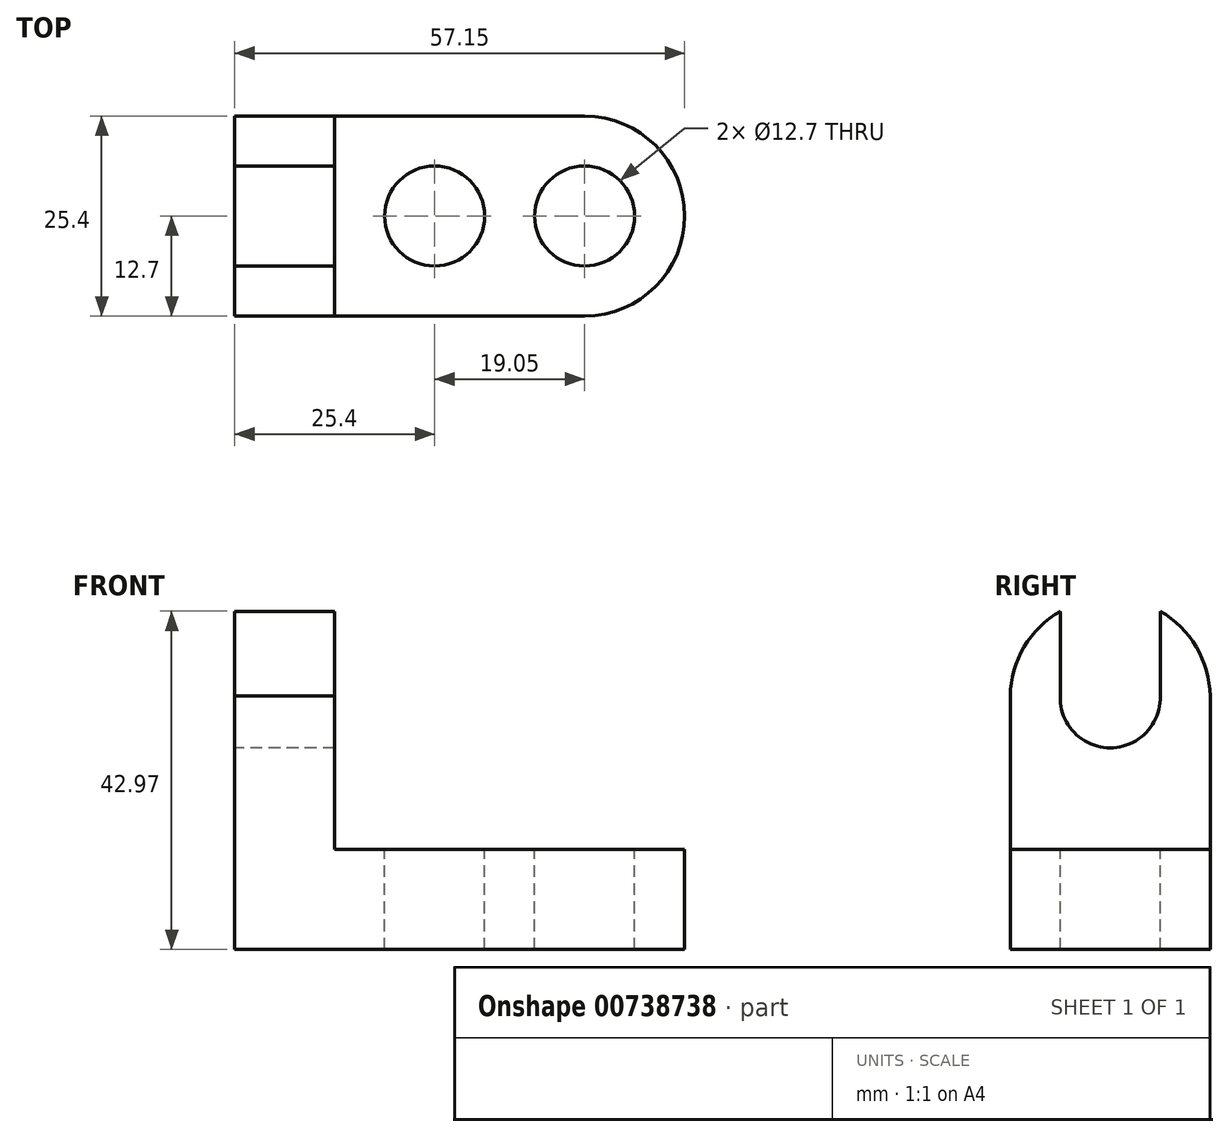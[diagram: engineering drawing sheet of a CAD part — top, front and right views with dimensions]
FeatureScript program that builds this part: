
annotation { "Feature Type Name" : "Feature", "Feature Type Description" : "" }
export const myFeature = defineFeature(function(context is Context, id is Id, definition is map)
    precondition{}
    {
        {
            var Q0;
            Q0=qCreatedBy(makeId("Front.planeOp"),FACE);
            var sketch = newSketch(context, id + "F0", { "sketchPlane" : qUnion([Q0])});
            skLineSegment(sketch, "E0", {"start": v(0, 0) * mm, "end": v(57.15, 0) * mm});
            skLineSegment(sketch, "E1", {"start": v(57.15, 0) * mm, "end": v(57.15, 12.7) * mm});
            skLineSegment(sketch, "E2", {"start": v(57.15, 12.7) * mm, "end": v(12.7, 12.7) * mm});
            skLineSegment(sketch, "E3", {"start": v(12.7, 12.7) * mm, "end": v(12.7, 44.45) * mm});
            skLineSegment(sketch, "E4", {"start": v(12.7, 44.45) * mm, "end": v(0, 44.45) * mm});
            skLineSegment(sketch, "E5", {"start": v(0, 44.45) * mm, "end": v(0, 0) * mm});
            skSolve(sketch);
        }
        {
            var Q0;
            Q0 = qSketchRegion(id + "F0", true);
            extrude(context, id + "F1", {"entities" : qUnion([Q0]), "depth" : 25.4 * mm, "offsetDistance" : 25.4 * mm});
        }
        {
            var Q0;
            Q0=makeQuery(id+"F1.opExtrude","SWEPT_FACE",FACE,{"disambiguationData":[OSD([sQuery(id+"F0.wireOp",EDGE,"E2")])]});
            var sketch = newSketch(context, id + "F2", { "sketchPlane" : qUnion([Q0])});
            skLineSegment(sketch, "E6", {"start": v(25.4, 0) * mm, "end": v(25.4, -25.4) * mm});
            skLineSegment(sketch, "E7", {"start": v(44.45, -25.4) * mm, "end": v(44.45, 0) * mm});
            skCircle(sketch, "E8", {"center": v(25.4, -12.7) * mm, "radius": 6.35 * mm});
            skCircle(sketch, "E9", {"center": v(44.45, -12.7) * mm, "radius": 6.35 * mm});
            skArc(sketch, "E10", {"start": v(44.45, -25.4) * mm, "mid": v(57.15, -12.7) * mm, "end": v(44.45, 0) * mm});
            skSolve(sketch);
        }
        {
            var Q0;
            {var subQ0=sQuery(id+"F2.wireOp",EDGE,"E8");var subQ1=sQuery(id+"F2.wireOp",EDGE,"E6");var subQ2=makeQuery(id+"F2.imprint","INTERSECT",VERTEX,{"disambiguationData":[OD(0.0)],"derivedFrom":[subQ1,subQ0]});Q0=makeQuery(id+"F2.imprint","IMPRINT",FACE,{"disambiguationData":[TD([[makeQuery(id+"F2.imprint","IMPRINT",EDGE,{"disambiguationData":[TD([[subQ2,-1.0]])],"derivedFrom":subQ1}),-1.0]])]});}
            var Q1;
            {var subQ0=sQuery(id+"F2.wireOp",EDGE,"E8");var subQ1=sQuery(id+"F2.wireOp",EDGE,"E6");var subQ2=makeQuery(id+"F2.imprint","INTERSECT",VERTEX,{"disambiguationData":[OD(0.0)],"derivedFrom":[subQ1,subQ0]});Q1=makeQuery(id+"F2.imprint","IMPRINT",FACE,{"disambiguationData":[TD([[makeQuery(id+"F2.imprint","IMPRINT",EDGE,{"disambiguationData":[TD([[subQ2,-1.0]])],"derivedFrom":subQ1}),1.0]])]});}
            var Q2;
            {var subQ0=sQuery(id+"F2.wireOp",EDGE,"E9");var subQ1=sQuery(id+"F2.wireOp",EDGE,"E7");var subQ2=makeQuery(id+"F2.imprint","INTERSECT",VERTEX,{"disambiguationData":[OD(0.0)],"derivedFrom":[subQ1,subQ0]});Q2=makeQuery(id+"F2.imprint","IMPRINT",FACE,{"disambiguationData":[TD([[makeQuery(id+"F2.imprint","IMPRINT",EDGE,{"disambiguationData":[TD([[subQ2,-1.0]])],"derivedFrom":subQ1}),1.0]])]});}
            var Q3;
            {var subQ0=sQuery(id+"F2.wireOp",EDGE,"E9");var subQ1=sQuery(id+"F2.wireOp",EDGE,"E7");var subQ2=makeQuery(id+"F2.imprint","INTERSECT",VERTEX,{"disambiguationData":[OD(0.0)],"derivedFrom":[subQ1,subQ0]});Q3=makeQuery(id+"F2.imprint","IMPRINT",FACE,{"disambiguationData":[TD([[makeQuery(id+"F2.imprint","IMPRINT",EDGE,{"disambiguationData":[TD([[subQ2,-1.0]])],"derivedFrom":subQ1}),-1.0]])]});}
            var Q4;
            {var subQ0=sQuery(id+"F2.wireOp",EDGE,"E10");var subQ1=sQuery(id+"F0.wireOp",EDGE,"E2");var subQ2=makeQuery(id+"F1.opExtrude","CAP_EDGE",EDGE,{"disambiguationData":[OSD([subQ1])],"isStart":true});var subQ3=makeQuery(id+"F2.imprint","INTERSECT",VERTEX,{"derivedFrom":[subQ2,sQuery(id+"F2.wireOp",EDGE,"E7"),subQ0]});Q4=makeQuery(id+"F2.imprint","IMPRINT",FACE,{"disambiguationData":[TD([[makeQuery(id+"F2.imprint","IMPRINT",EDGE,{"disambiguationData":[TD([[subQ3,1.0]])],"derivedFrom":subQ0}),-1.0]])]});}
            var Q5;
            {var subQ0=sQuery(id+"F2.wireOp",EDGE,"E10");var subQ1=sQuery(id+"F0.wireOp",EDGE,"E2");var subQ2=makeQuery(id+"F1.opExtrude","CAP_EDGE",EDGE,{"disambiguationData":[OSD([subQ1])],"isStart":false});var subQ3=makeQuery(id+"F2.imprint","INTERSECT",VERTEX,{"derivedFrom":[subQ2,sQuery(id+"F2.wireOp",EDGE,"E7"),subQ0]});Q5=makeQuery(id+"F2.imprint","IMPRINT",FACE,{"disambiguationData":[TD([[makeQuery(id+"F2.imprint","IMPRINT",EDGE,{"disambiguationData":[TD([[subQ3,-1.0]])],"derivedFrom":subQ0}),-1.0]])]});}
            extrude(context, id + "F3", {"entities" : qUnion([Q0, Q1, Q2, Q3, Q4, Q5]), "operationType" : NewBodyOperationType.REMOVE, "endBound" : BoundingType.THROUGH_ALL, "oppositeDirection" : true, "depth" : 25.4 * mm, "offsetDistance" : 25.4 * mm});
        }
        {
            var Q0;
            Q0=makeQuery(id+"F1.opExtrude","SWEPT_FACE",FACE,{"disambiguationData":[OSD([sQuery(id+"F0.wireOp",EDGE,"E3")])]});
            var sketch = newSketch(context, id + "F4", { "sketchPlane" : qUnion([Q0])});
            skLineSegment(sketch, "E11", {"start": v(-25.4, 31.75) * mm, "end": v(0, 31.75) * mm});
            skArc(sketch, "E12", {"start": v(0, 31.75) * mm, "mid": v(-12.7, 44.67) * mm, "end": v(-25.4, 31.75) * mm});
            skSolve(sketch);
        }
        {
            var Q0;
            {var subQ0=sQuery(id+"F4.wireOp",EDGE,"E12");var subQ1=makeQuery(id+"F1.opExtrude","CAP_EDGE",EDGE,{"disambiguationData":[OSD([sQuery(id+"F0.wireOp",EDGE,"E3")])],"isStart":true});var subQ3=makeQuery(id+"F4.imprint","INTERSECT",VERTEX,{"derivedFrom":[subQ1,subQ0]});Q0=makeQuery(id+"F4.imprint","IMPRINT",FACE,{"disambiguationData":[TD([[makeQuery(id+"F4.imprint","IMPRINT",EDGE,{"disambiguationData":[TD([[subQ3,1.0]])],"derivedFrom":subQ0}),1.0]])]});}
            var Q1;
            {var subQ0=sQuery(id+"F4.wireOp",EDGE,"E12");var subQ1=makeQuery(id+"F1.opExtrude","SWEPT_EDGE",EDGE,{"disambiguationData":[OSD([sQuery(id+"F0.wireOp",EDGE,"E3"),sQuery(id+"F0.wireOp",EDGE,"E4")])]});var subQ2=makeQuery(id+"F4.imprint","INTERSECT",VERTEX,{"disambiguationData":[OD(0.0)],"derivedFrom":[subQ1,subQ0]});Q1=makeQuery(id+"F4.imprint","IMPRINT",FACE,{"disambiguationData":[TD([[makeQuery(id+"F4.imprint","IMPRINT",EDGE,{"disambiguationData":[TD([[subQ2,-1.0]])],"derivedFrom":subQ0}),1.0]])]});}
            var Q2;
            {var subQ0=sQuery(id+"F4.wireOp",EDGE,"E12");var subQ1=makeQuery(id+"F1.opExtrude","CAP_EDGE",EDGE,{"disambiguationData":[OSD([sQuery(id+"F0.wireOp",EDGE,"E3")])],"isStart":false});var subQ3=makeQuery(id+"F4.imprint","INTERSECT",VERTEX,{"derivedFrom":[subQ1,subQ0]});Q2=makeQuery(id+"F4.imprint","IMPRINT",FACE,{"disambiguationData":[TD([[makeQuery(id+"F4.imprint","IMPRINT",EDGE,{"disambiguationData":[TD([[subQ3,-1.0]])],"derivedFrom":subQ0}),1.0]])]});}
            var Q3;
            {var subQ0=sQuery(id+"F4.wireOp",EDGE,"E12");var subQ1=sQuery(id+"F0.wireOp",EDGE,"E3");var subQ4=makeQuery(id+"F1.opExtrude","CAP_EDGE",EDGE,{"disambiguationData":[OSD([subQ1])],"isStart":false});var subQ5=makeQuery(id+"F4.imprint","INTERSECT",VERTEX,{"derivedFrom":[subQ4,subQ0]});Q3=makeQuery(id+"F4.imprint","IMPRINT",FACE,{"disambiguationData":[TD([[makeQuery(id+"F4.imprint","IMPRINT",EDGE,{"disambiguationData":[TD([[subQ5,1.0]])],"derivedFrom":subQ0}),-1.0]])]});}
            var Q4;
            {var subQ0=sQuery(id+"F4.wireOp",EDGE,"E12");var subQ1=sQuery(id+"F0.wireOp",EDGE,"E3");var subQ2=makeQuery(id+"F1.opExtrude","CAP_EDGE",EDGE,{"disambiguationData":[OSD([subQ1])],"isStart":true});var subQ3=makeQuery(id+"F4.imprint","INTERSECT",VERTEX,{"derivedFrom":[subQ2,subQ0]});Q4=makeQuery(id+"F4.imprint","IMPRINT",FACE,{"disambiguationData":[TD([[makeQuery(id+"F4.imprint","IMPRINT",EDGE,{"disambiguationData":[TD([[subQ3,-1.0]])],"derivedFrom":subQ0}),-1.0]])]});}
            extrude(context, id + "F5", {"entities" : qUnion([Q0, Q1, Q2, Q3, Q4]), "operationType" : NewBodyOperationType.REMOVE, "endBound" : BoundingType.THROUGH_ALL, "oppositeDirection" : true, "depth" : 25.4 * mm, "offsetDistance" : 25.4 * mm});
        }
        {
            var Q0;
            Q0=makeQuery(id+"F1.opExtrude","SWEPT_FACE",FACE,{"disambiguationData":[OSD([sQuery(id+"F0.wireOp",EDGE,"E5")])]});
            var sketch = newSketch(context, id + "F6", { "sketchPlane" : qUnion([Q0])});
            skLineSegment(sketch, "E13", {"start": v(0, 31.75) * mm, "end": v(25.4, 31.75) * mm});
            skCircle(sketch, "E14", {"center": v(12.7, 31.96) * mm, "radius": 6.35 * mm});
            skLineSegment(sketch, "E15", {"start": v(6.35, 31.75) * mm, "end": v(6.35, 42.97) * mm});
            skLineSegment(sketch, "E16", {"start": v(19.05, 31.75) * mm, "end": v(19.05, 42.97) * mm});
            skSolve(sketch);
        }
        {
            var Q0;
            Q0 = qSketchRegion(id + "F6", true);
            var Q1;
            {var subQ0=sQuery(id+"F0.wireOp",EDGE,"E5");var subQ1=sQuery(id+"F0.wireOp",EDGE,"E4");var subQ2=makeQuery(id+"F1.opExtrude","SWEPT_EDGE",EDGE,{"disambiguationData":[OSD([subQ1,subQ0])]});Q1=makeQuery(id+"F6.imprint","IMPRINT",FACE,{"disambiguationData":[TD([[makeQuery(id+"F6.imprint","IMPRINT",EDGE,{"derivedFrom":subQ2}),1.0]])]});}
            extrude(context, id + "F7", {"entities" : qUnion([Q0, Q1]), "operationType" : NewBodyOperationType.REMOVE, "endBound" : BoundingType.THROUGH_ALL, "oppositeDirection" : true, "depth" : 25.4 * mm, "offsetDistance" : 25.4 * mm});
        }
    });
